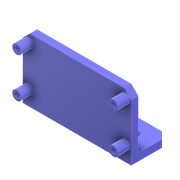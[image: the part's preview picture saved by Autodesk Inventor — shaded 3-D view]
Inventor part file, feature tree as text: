
AUTODESK INVENTOR PART (.ipt)
format: ipt  version: 2022 (Build 260153000, 153)  size: 189,440 bytes
history: native  units: mm
features: sketch x5, extrude x3, hole x2, projected_geometry x2, chamfer x1
ambient origin geometry x8: Origin, YZ Plane, XZ Plane, XY Plane, X Axis, Y Axis, Z Axis, Center Point
bodies: Solid1 (feature_tree)
feature tree (13):
  extrude  "Extrusion1"  Depth=44.0mm
  extrude  "Extrusion2"  Depth=3.0mm TaperAngle=0.0deg
  hole  "Hole1"  [1 undecoded]
  hole  "Hole2"  [1 undecoded]
  chamfer  "Chamfer2"  Distance=3.0mm Angle=45.0deg
  extrude  "Extrusion3"  Depth=2.0mm
  sketch  "Sketch1"  dims[d0=20.0mm d1=44.0mm]
  sketch  "Sketch2"  dims[d2=2.0mm d3=3.0mm d4=0.0mm]
  sketch  "Sketch3"  dims[d6=3.0mm d7=0.0mm d8=2.0mm]
  sketch  "Sketch5"  dims[d9=2.0mm d10=2.0mm]
  sketch  "Sketch6"  dims[d11=2.0mm d14=2.4mm d15=6.0mm d16=4.0mm d17=2.0mm d18=90.0deg d19=6.0mm d20=0.0mm d33=3.4mm d34=6.0mm d35=4.0mm d36=2.0mm d37=90.0deg d38=6.0mm d39=0.0mm d40=3.0mm d41=2.0mm d42=45.0deg d43=0.5mm d44=44.0mm d45=20.0mm d46=4.0mm d47=4.0mm d49=4.0mm d50=4.0mm d51=5.0mm d52=0.0mm d54=46.0mm d55=16.0mm d56=13.0mm d57=6.5mm d58=30.0mm d59=46.0mm d60=2.0mm d61=1.0mm d62=1.0mm]
  projected_geometry  "Project Cut Edges2"
  projected_geometry  "Project Cut Edges3"
note: 2 required parameter values undecoded (feature->parameter linkage not recoverable at this tier; creation-order binding heuristic only, values carry confidence <= 0.55)
